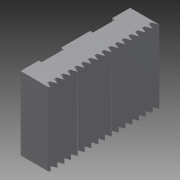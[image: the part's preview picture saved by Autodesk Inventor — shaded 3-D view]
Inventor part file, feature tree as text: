
AUTODESK INVENTOR PART (.ipt)
format: ipt  version: 2011 (Build 150239000, 239)  size: 188,416 bytes
history: native  units: mm
features: extrude x2, sketch x2
ambient origin geometry x8: Origin, YZ Plane, XZ Plane, XY Plane, X Axis, Y Axis, Z Axis, Center Point
bodies: Solid1 (feature_tree)
feature tree (4):
  extrude  "Extrusion1"  Depth=15.0mm
  extrude  "Extrusion4"  Depth=2.99mm
  sketch  "Sketch1"  dims[d0=4.0mm d1=15.0mm]
  sketch  "Sketch6"  dims[d2=0.389mm d3=2.99mm d4=4.0mm d5=2.5mm d6=3.01mm d7=10.0mm d8=0.0mm d14=15.812777mm d15=3.490659mm d16=8.011807mm d17=10.541851mm d24=15.812777mm d25=3.490659mm d26=8.011807mm d27=10.541851mm d35=15.812777mm d36=3.490659mm d37=8.011807mm d38=10.541851mm d59=3.355575mm d60=3.490659mm d61=2.550237mm d62=3.355575mm d70=0.0mm d71=0.0mm d72=12.217305mm d73=0.805338mm d74=12.217305mm d76=0.169696mm d77=19.198622mm d78=12.217305mm d79=6.981317mm d80=0.92563mm d81=0.0025mm d82=0.0025mm d83=0.0025mm d84=0.0025mm d85=10.0mm d86=0.0mm d87=0.0025mm]
